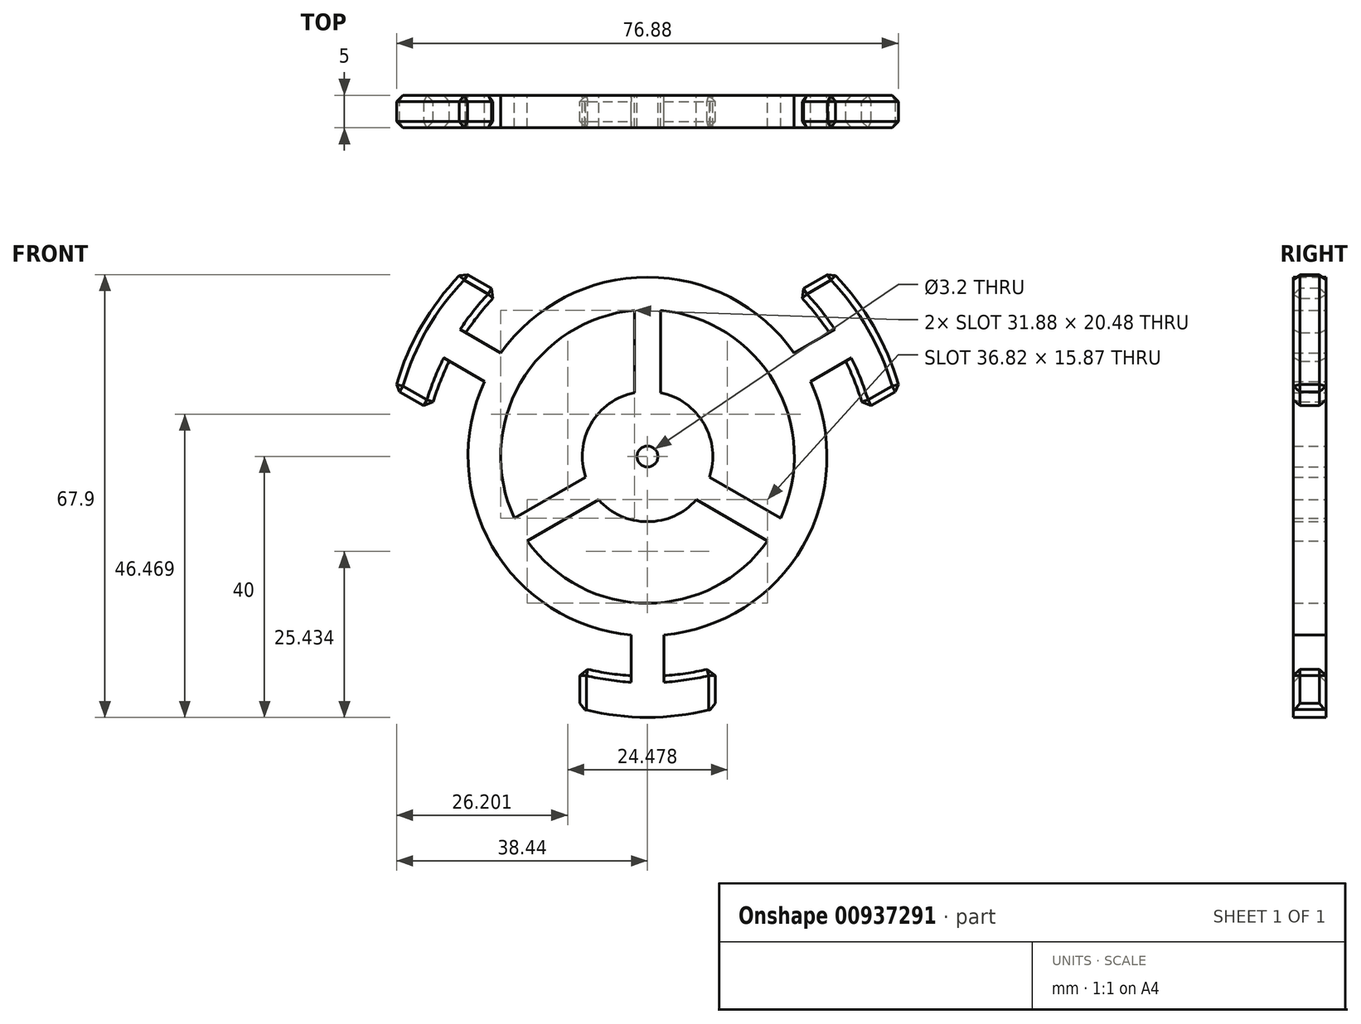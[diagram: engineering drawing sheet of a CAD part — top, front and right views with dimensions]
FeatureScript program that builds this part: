
annotation { "Feature Type Name" : "Feature", "Feature Type Description" : "" }
export const myFeature = defineFeature(function(context is Context, id is Id, definition is map)
    precondition{}
    {
        {
            var Q0;
            Q0=qCreatedBy(makeId("Front.planeOp"),FACE);
            var sketch = newSketch(context, id + "F0", { "sketchPlane" : qUnion([Q0])});
            skCircle(sketch, "E0", {"center": v(0, 0) * mm, "radius": 1.6 * mm});
            skCircle(sketch, "E1", {"center": v(0, 0) * mm, "radius": 10 * mm});
            skArc(sketch, "E2", {"start": v(20.4, -9.47) * mm, "mid": v(19.49, 11.25) * mm, "end": v(2, 22.41) * mm});
            skLineSegment(sketch, "E3", {"start": v(-2, 9.8) * mm, "end": v(-2, 22.41) * mm});
            skLineSegment(sketch, "E4", {"start": v(2, 9.8) * mm, "end": v(2, 22.41) * mm});
            skLineSegment(sketch, "E5", {"start": v(-9.49, -3.17) * mm, "end": v(-20.4, -9.47) * mm});
            skLineSegment(sketch, "E6", {"start": v(-7.49, -6.63) * mm, "end": v(-18.4, -12.94) * mm});
            skLineSegment(sketch, "E7", {"start": v(7.49, -6.63) * mm, "end": v(18.4, -12.94) * mm});
            skLineSegment(sketch, "E8", {"start": v(9.49, -3.17) * mm, "end": v(20.4, -9.47) * mm});
            skArc(sketch, "E9.trimOffspring", {"start": v(-2, 22.41) * mm, "mid": v(-19.49, 11.25) * mm, "end": v(-20.4, -9.47) * mm});
            skArc(sketch, "E10.trimOffspring", {"start": v(-18.4, -12.94) * mm, "mid": v(0, -22.5) * mm, "end": v(18.4, -12.94) * mm});
            skLineSegment(sketch, "E11", {"start": v(-2.5, -27.39) * mm, "end": v(-2.5, -33.61) * mm});
            skLineSegment(sketch, "E12", {"start": v(2.5, -27.39) * mm, "end": v(2.5, -33.61) * mm});
            skArc(sketch, "E13", {"start": v(-10.37, -38.63) * mm, "mid": v(0, -40) * mm, "end": v(10.37, -38.63) * mm});
            skLineSegment(sketch, "E14", {"start": v(-10.37, -38.63) * mm, "end": v(-10.37, -32.32) * mm});
            skLineSegment(sketch, "E15", {"start": v(10.37, -38.63) * mm, "end": v(10.37, -32.32) * mm});
            skArc(sketch, "E16", {"start": v(-10.37, -32.32) * mm, "mid": v(0, -33.7) * mm, "end": v(10.37, -32.32) * mm});
            skCircle(sketch, "E17", {"center": v(0, 0) * mm, "radius": 27.5 * mm});
            skLineSegment(sketch, "E18", {"start": v(24.97, 11.52) * mm, "end": v(30.37, 14.63) * mm});
            skLineSegment(sketch, "E19", {"start": v(22.47, 15.85) * mm, "end": v(27.87, 18.96) * mm});
            skLineSegment(sketch, "E20", {"start": v(38.65, 10.32) * mm, "end": v(33.18, 7.17) * mm});
            skLineSegment(sketch, "E21", {"start": v(28.28, 28.3) * mm, "end": v(22.82, 25.14) * mm});
            skArc(sketch, "E22", {"start": v(33.18, 7.17) * mm, "mid": v(29.18, 16.84) * mm, "end": v(22.82, 25.14) * mm});
            skArc(sketch, "E23", {"start": v(38.65, 10.32) * mm, "mid": v(34.65, 19.99) * mm, "end": v(28.28, 28.3) * mm});
            skLineSegment(sketch, "E24", {"start": v(-24.97, 11.52) * mm, "end": v(-30.37, 14.63) * mm});
            skLineSegment(sketch, "E25", {"start": v(-22.47, 15.85) * mm, "end": v(-27.87, 18.96) * mm});
            skLineSegment(sketch, "E26", {"start": v(-28.28, 28.3) * mm, "end": v(-22.82, 25.14) * mm});
            skLineSegment(sketch, "E27", {"start": v(-38.65, 10.32) * mm, "end": v(-33.18, 7.17) * mm});
            skArc(sketch, "E28", {"start": v(-22.82, 25.14) * mm, "mid": v(-29.18, 16.84) * mm, "end": v(-33.18, 7.17) * mm});
            skArc(sketch, "E29", {"start": v(-28.28, 28.3) * mm, "mid": v(-34.65, 19.99) * mm, "end": v(-38.65, 10.32) * mm});
            skSolve(sketch);
        }
        {
            var Q0;
            Q0=makeQuery(id+"F0.imprint","IMPRINT",FACE,{"disambiguationData":[TD([[makeQuery(id+"F0.imprint","IMPRINT",EDGE,{"derivedFrom":sQuery(id+"F0.wireOp",EDGE,"E2")}),-1.0]])]});
            var Q1;
            Q1=makeQuery(id+"F0.imprint","IMPRINT",FACE,{"disambiguationData":[TD([[makeQuery(id+"F0.imprint","IMPRINT",EDGE,{"derivedFrom":sQuery(id+"F0.wireOp",EDGE,"E0")}),-1.0]])]});
            var Q2;
            {var subQ0=sQuery(id+"F0.wireOp",EDGE,"E11");Q2=makeQuery(id+"F0.imprint","IMPRINT",FACE,{"disambiguationData":[TD([[makeQuery(id+"F0.imprint","IMPRINT",EDGE,{"derivedFrom":subQ0}),1.0]])]});}
            var Q3;
            {var subQ3=sQuery(id+"F0.wireOp",EDGE,"E14");Q3=makeQuery(id+"F0.imprint","IMPRINT",FACE,{"disambiguationData":[TD([[makeQuery(id+"F0.imprint","IMPRINT",EDGE,{"derivedFrom":subQ3}),-1.0]])]});}
            var Q4;
            {var subQ2=sQuery(id+"F0.wireOp",EDGE,"E20");Q4=makeQuery(id+"F0.imprint","IMPRINT",FACE,{"disambiguationData":[TD([[makeQuery(id+"F0.imprint","IMPRINT",EDGE,{"derivedFrom":subQ2}),-1.0]])]});}
            var Q5;
            {var subQ0=sQuery(id+"F0.wireOp",EDGE,"E18");Q5=makeQuery(id+"F0.imprint","IMPRINT",FACE,{"disambiguationData":[TD([[makeQuery(id+"F0.imprint","IMPRINT",EDGE,{"derivedFrom":subQ0}),1.0]])]});}
            var Q6;
            {var subQ3=sQuery(id+"F0.wireOp",EDGE,"E26");Q6=makeQuery(id+"F0.imprint","IMPRINT",FACE,{"disambiguationData":[TD([[makeQuery(id+"F0.imprint","IMPRINT",EDGE,{"derivedFrom":subQ3}),-1.0]])]});}
            var Q7;
            {var subQ0=sQuery(id+"F0.wireOp",EDGE,"E24");Q7=makeQuery(id+"F0.imprint","IMPRINT",FACE,{"disambiguationData":[TD([[makeQuery(id+"F0.imprint","IMPRINT",EDGE,{"derivedFrom":subQ0}),-1.0]])]});}
            extrude(context, id + "F1", {"entities" : qUnion([Q0, Q1, Q2, Q3, Q4, Q5, Q6, Q7]), "depth" : 5 * mm, "offsetDistance" : 25 * mm});
        }
        {
            var Q0;
            Q0=makeQuery(id+"F1.opExtrude","SWEPT_EDGE",EDGE,{"disambiguationData":[OSD([sQuery(id+"F0.wireOp",EDGE,"E20"),sQuery(id+"F0.wireOp",EDGE,"E23")])]});
            var Q1;
            Q1=makeQuery(id+"F1.opExtrude","SWEPT_EDGE",EDGE,{"disambiguationData":[OSD([sQuery(id+"F0.wireOp",EDGE,"E21"),sQuery(id+"F0.wireOp",EDGE,"E23")])]});
            var Q2;
            Q2=makeQuery(id+"F1.opExtrude","CAP_EDGE",EDGE,{"disambiguationData":[OSD([sQuery(id+"F0.wireOp",EDGE,"E20")])],"isStart":false});
            var Q3;
            Q3=makeQuery(id+"F1.opExtrude","SWEPT_EDGE",EDGE,{"disambiguationData":[OSD([sQuery(id+"F0.wireOp",EDGE,"E20"),sQuery(id+"F0.wireOp",EDGE,"E22")])]});
            var Q4;
            Q4=makeQuery(id+"F1.opExtrude","CAP_EDGE",EDGE,{"disambiguationData":[OSD([sQuery(id+"F0.wireOp",EDGE,"E20")])],"isStart":true});
            var Q5;
            Q5=makeQuery(id+"F1.opExtrude","CAP_EDGE",EDGE,{"disambiguationData":[OSD([sQuery(id+"F0.wireOp",EDGE,"E21")])],"isStart":false});
            var Q6;
            Q6=makeQuery(id+"F1.opExtrude","CAP_EDGE",EDGE,{"disambiguationData":[OSD([sQuery(id+"F0.wireOp",EDGE,"E23")])],"isStart":true});
            var Q7;
            Q7=makeQuery(id+"F1.opExtrude","CAP_EDGE",EDGE,{"disambiguationData":[OSD([sQuery(id+"F0.wireOp",EDGE,"E21")])],"isStart":true});
            var Q8;
            {var subQ0=sQuery(id+"F0.wireOp",EDGE,"E22");Q8=makeQuery(id+"F1.opExtrude","CAP_EDGE",EDGE,{"disambiguationData":[OSD([subQ0]),TDD([makeQuery(id+"F0.imprint","IMPRINT",EDGE,{"disambiguationData":[TD([[makeQuery(id+"F0.imprint","INTERSECT",VERTEX,{"derivedFrom":[sQuery(id+"F0.wireOp",EDGE,"E21"),subQ0]}),1.0]])],"derivedFrom":subQ0})])],"isStart":true});}
            var Q9;
            {var subQ0=sQuery(id+"F0.wireOp",EDGE,"E22");Q9=makeQuery(id+"F1.opExtrude","CAP_EDGE",EDGE,{"disambiguationData":[OSD([subQ0]),TDD([makeQuery(id+"F0.imprint","IMPRINT",EDGE,{"disambiguationData":[TD([[makeQuery(id+"F0.imprint","INTERSECT",VERTEX,{"derivedFrom":[sQuery(id+"F0.wireOp",EDGE,"E18"),subQ0]}),1.0]])],"derivedFrom":subQ0})])],"isStart":true});}
            var Q10;
            Q10=makeQuery(id+"F1.opExtrude","SWEPT_EDGE",EDGE,{"disambiguationData":[OSD([sQuery(id+"F0.wireOp",EDGE,"E21"),sQuery(id+"F0.wireOp",EDGE,"E22")])]});
            var Q11;
            Q11=makeQuery(id+"F1.opExtrude","CAP_EDGE",EDGE,{"disambiguationData":[OSD([sQuery(id+"F0.wireOp",EDGE,"E23")])],"isStart":false});
            var Q12;
            Q12=makeQuery(id+"F1.opExtrude","SWEPT_EDGE",EDGE,{"disambiguationData":[OSD([sQuery(id+"F0.wireOp",EDGE,"E27"),sQuery(id+"F0.wireOp",EDGE,"E29")])]});
            var Q13;
            Q13=makeQuery(id+"F1.opExtrude","SWEPT_EDGE",EDGE,{"disambiguationData":[OSD([sQuery(id+"F0.wireOp",EDGE,"E27"),sQuery(id+"F0.wireOp",EDGE,"E28")])]});
            var Q14;
            Q14=makeQuery(id+"F1.opExtrude","CAP_EDGE",EDGE,{"disambiguationData":[OSD([sQuery(id+"F0.wireOp",EDGE,"E27")])],"isStart":false});
            var Q15;
            Q15=makeQuery(id+"F1.opExtrude","CAP_EDGE",EDGE,{"disambiguationData":[OSD([sQuery(id+"F0.wireOp",EDGE,"E27")])],"isStart":true});
            var Q16;
            Q16=makeQuery(id+"F1.opExtrude","CAP_EDGE",EDGE,{"disambiguationData":[OSD([sQuery(id+"F0.wireOp",EDGE,"E29")])],"isStart":true});
            var Q17;
            Q17=makeQuery(id+"F1.opExtrude","CAP_EDGE",EDGE,{"disambiguationData":[OSD([sQuery(id+"F0.wireOp",EDGE,"E29")])],"isStart":false});
            var Q18;
            {var subQ0=sQuery(id+"F0.wireOp",EDGE,"E28");Q18=makeQuery(id+"F1.opExtrude","CAP_EDGE",EDGE,{"disambiguationData":[OSD([subQ0]),TDD([makeQuery(id+"F0.imprint","IMPRINT",EDGE,{"disambiguationData":[TD([[makeQuery(id+"F0.imprint","INTERSECT",VERTEX,{"derivedFrom":[sQuery(id+"F0.wireOp",EDGE,"E24"),subQ0]}),-1.0]])],"derivedFrom":subQ0})])],"isStart":true});}
            var Q19;
            {var subQ0=sQuery(id+"F0.wireOp",EDGE,"E28");Q19=makeQuery(id+"F1.opExtrude","CAP_EDGE",EDGE,{"disambiguationData":[OSD([subQ0]),TDD([makeQuery(id+"F0.imprint","IMPRINT",EDGE,{"disambiguationData":[TD([[makeQuery(id+"F0.imprint","INTERSECT",VERTEX,{"derivedFrom":[sQuery(id+"F0.wireOp",EDGE,"E26"),subQ0]}),-1.0]])],"derivedFrom":subQ0})])],"isStart":true});}
            var Q20;
            Q20=makeQuery(id+"F1.opExtrude","CAP_EDGE",EDGE,{"disambiguationData":[OSD([sQuery(id+"F0.wireOp",EDGE,"E26")])],"isStart":true});
            var Q21;
            Q21=makeQuery(id+"F1.opExtrude","CAP_EDGE",EDGE,{"disambiguationData":[OSD([sQuery(id+"F0.wireOp",EDGE,"E26")])],"isStart":false});
            var Q22;
            {var subQ0=sQuery(id+"F0.wireOp",EDGE,"E28");Q22=makeQuery(id+"F1.opExtrude","CAP_EDGE",EDGE,{"disambiguationData":[OSD([subQ0]),TDD([makeQuery(id+"F0.imprint","IMPRINT",EDGE,{"disambiguationData":[TD([[makeQuery(id+"F0.imprint","INTERSECT",VERTEX,{"derivedFrom":[sQuery(id+"F0.wireOp",EDGE,"E26"),subQ0]}),-1.0]])],"derivedFrom":subQ0})])],"isStart":false});}
            var Q23;
            {var subQ0=sQuery(id+"F0.wireOp",EDGE,"E28");Q23=makeQuery(id+"F1.opExtrude","CAP_EDGE",EDGE,{"disambiguationData":[OSD([subQ0]),TDD([makeQuery(id+"F0.imprint","IMPRINT",EDGE,{"disambiguationData":[TD([[makeQuery(id+"F0.imprint","INTERSECT",VERTEX,{"derivedFrom":[sQuery(id+"F0.wireOp",EDGE,"E24"),subQ0]}),-1.0]])],"derivedFrom":subQ0})])],"isStart":false});}
            var Q24;
            Q24=makeQuery(id+"F1.opExtrude","SWEPT_EDGE",EDGE,{"disambiguationData":[OSD([sQuery(id+"F0.wireOp",EDGE,"E26"),sQuery(id+"F0.wireOp",EDGE,"E29")])]});
            var Q25;
            Q25=makeQuery(id+"F1.opExtrude","SWEPT_EDGE",EDGE,{"disambiguationData":[OSD([sQuery(id+"F0.wireOp",EDGE,"E26"),sQuery(id+"F0.wireOp",EDGE,"E28")])]});
            var Q26;
            Q26=makeQuery(id+"F1.opExtrude","SWEPT_EDGE",EDGE,{"disambiguationData":[OSD([sQuery(id+"F0.wireOp",EDGE,"E15"),sQuery(id+"F0.wireOp",EDGE,"E13")])]});
            var Q27;
            Q27=makeQuery(id+"F1.opExtrude","CAP_EDGE",EDGE,{"disambiguationData":[OSD([sQuery(id+"F0.wireOp",EDGE,"E15")])],"isStart":true});
            var Q28;
            Q28=makeQuery(id+"F1.opExtrude","SWEPT_EDGE",EDGE,{"disambiguationData":[OSD([sQuery(id+"F0.wireOp",EDGE,"E15"),sQuery(id+"F0.wireOp",EDGE,"E16")])]});
            var Q29;
            Q29=makeQuery(id+"F1.opExtrude","CAP_EDGE",EDGE,{"disambiguationData":[OSD([sQuery(id+"F0.wireOp",EDGE,"E15")])],"isStart":false});
            var Q30;
            Q30=makeQuery(id+"F1.opExtrude","CAP_EDGE",EDGE,{"disambiguationData":[OSD([sQuery(id+"F0.wireOp",EDGE,"E13")])],"isStart":false});
            var Q31;
            {var subQ0=sQuery(id+"F0.wireOp",EDGE,"E16");Q31=makeQuery(id+"F1.opExtrude","CAP_EDGE",EDGE,{"disambiguationData":[OSD([subQ0]),TDD([makeQuery(id+"F0.imprint","IMPRINT",EDGE,{"disambiguationData":[TD([[makeQuery(id+"F0.imprint","INTERSECT",VERTEX,{"derivedFrom":[sQuery(id+"F0.wireOp",EDGE,"E12"),subQ0]}),-1.0]])],"derivedFrom":subQ0})])],"isStart":false});}
            var Q32;
            {var subQ0=sQuery(id+"F0.wireOp",EDGE,"E16");Q32=makeQuery(id+"F1.opExtrude","CAP_EDGE",EDGE,{"disambiguationData":[OSD([subQ0]),TDD([makeQuery(id+"F0.imprint","IMPRINT",EDGE,{"disambiguationData":[TD([[makeQuery(id+"F0.imprint","INTERSECT",VERTEX,{"derivedFrom":[sQuery(id+"F0.wireOp",EDGE,"E11"),subQ0]}),1.0]])],"derivedFrom":subQ0})])],"isStart":false});}
            var Q33;
            Q33=makeQuery(id+"F1.opExtrude","CAP_EDGE",EDGE,{"disambiguationData":[OSD([sQuery(id+"F0.wireOp",EDGE,"E14")])],"isStart":false});
            var Q34;
            Q34=makeQuery(id+"F1.opExtrude","SWEPT_EDGE",EDGE,{"disambiguationData":[OSD([sQuery(id+"F0.wireOp",EDGE,"E14"),sQuery(id+"F0.wireOp",EDGE,"E16")])]});
            var Q35;
            Q35=makeQuery(id+"F1.opExtrude","CAP_EDGE",EDGE,{"disambiguationData":[OSD([sQuery(id+"F0.wireOp",EDGE,"E14")])],"isStart":true});
            var Q36;
            Q36=makeQuery(id+"F1.opExtrude","SWEPT_EDGE",EDGE,{"disambiguationData":[OSD([sQuery(id+"F0.wireOp",EDGE,"E14"),sQuery(id+"F0.wireOp",EDGE,"E13")])]});
            var Q37;
            Q37=makeQuery(id+"F1.opExtrude","CAP_EDGE",EDGE,{"disambiguationData":[OSD([sQuery(id+"F0.wireOp",EDGE,"E13")])],"isStart":true});
            var Q38;
            {var subQ0=sQuery(id+"F0.wireOp",EDGE,"E16");Q38=makeQuery(id+"F1.opExtrude","CAP_EDGE",EDGE,{"disambiguationData":[OSD([subQ0]),TDD([makeQuery(id+"F0.imprint","IMPRINT",EDGE,{"disambiguationData":[TD([[makeQuery(id+"F0.imprint","INTERSECT",VERTEX,{"derivedFrom":[sQuery(id+"F0.wireOp",EDGE,"E12"),subQ0]}),-1.0]])],"derivedFrom":subQ0})])],"isStart":true});}
            var Q39;
            {var subQ0=sQuery(id+"F0.wireOp",EDGE,"E16");Q39=makeQuery(id+"F1.opExtrude","CAP_EDGE",EDGE,{"disambiguationData":[OSD([subQ0]),TDD([makeQuery(id+"F0.imprint","IMPRINT",EDGE,{"disambiguationData":[TD([[makeQuery(id+"F0.imprint","INTERSECT",VERTEX,{"derivedFrom":[sQuery(id+"F0.wireOp",EDGE,"E11"),subQ0]}),1.0]])],"derivedFrom":subQ0})])],"isStart":true});}
            var Q40;
            {var subQ0=sQuery(id+"F0.wireOp",EDGE,"E22");Q40=makeQuery(id+"F1.opExtrude","CAP_EDGE",EDGE,{"disambiguationData":[OSD([subQ0]),TDD([makeQuery(id+"F0.imprint","IMPRINT",EDGE,{"disambiguationData":[TD([[makeQuery(id+"F0.imprint","INTERSECT",VERTEX,{"derivedFrom":[sQuery(id+"F0.wireOp",EDGE,"E21"),subQ0]}),1.0]])],"derivedFrom":subQ0})])],"isStart":false});}
            var Q41;
            {var subQ0=sQuery(id+"F0.wireOp",EDGE,"E22");Q41=makeQuery(id+"F1.opExtrude","CAP_EDGE",EDGE,{"disambiguationData":[OSD([subQ0]),TDD([makeQuery(id+"F0.imprint","IMPRINT",EDGE,{"disambiguationData":[TD([[makeQuery(id+"F0.imprint","INTERSECT",VERTEX,{"derivedFrom":[sQuery(id+"F0.wireOp",EDGE,"E18"),subQ0]}),1.0]])],"derivedFrom":subQ0})])],"isStart":false});}
            chamfer(context, id + "F2", {"entities" : qUnion([Q0, Q1, Q2, Q3, Q4, Q5, Q6, Q7, Q8, Q9, Q10, Q11, Q12, Q13, Q14, Q15, Q16, Q17, Q18, Q19, Q20, Q21, Q22, Q23, Q24, Q25, Q26, Q27, Q28, Q29, Q30, Q31, Q32, Q33, Q34, Q35, Q36, Q37, Q38, Q39, Q40, Q41]), "width" : 1 * mm, "tangentPropagation" : true});
        }
    });
